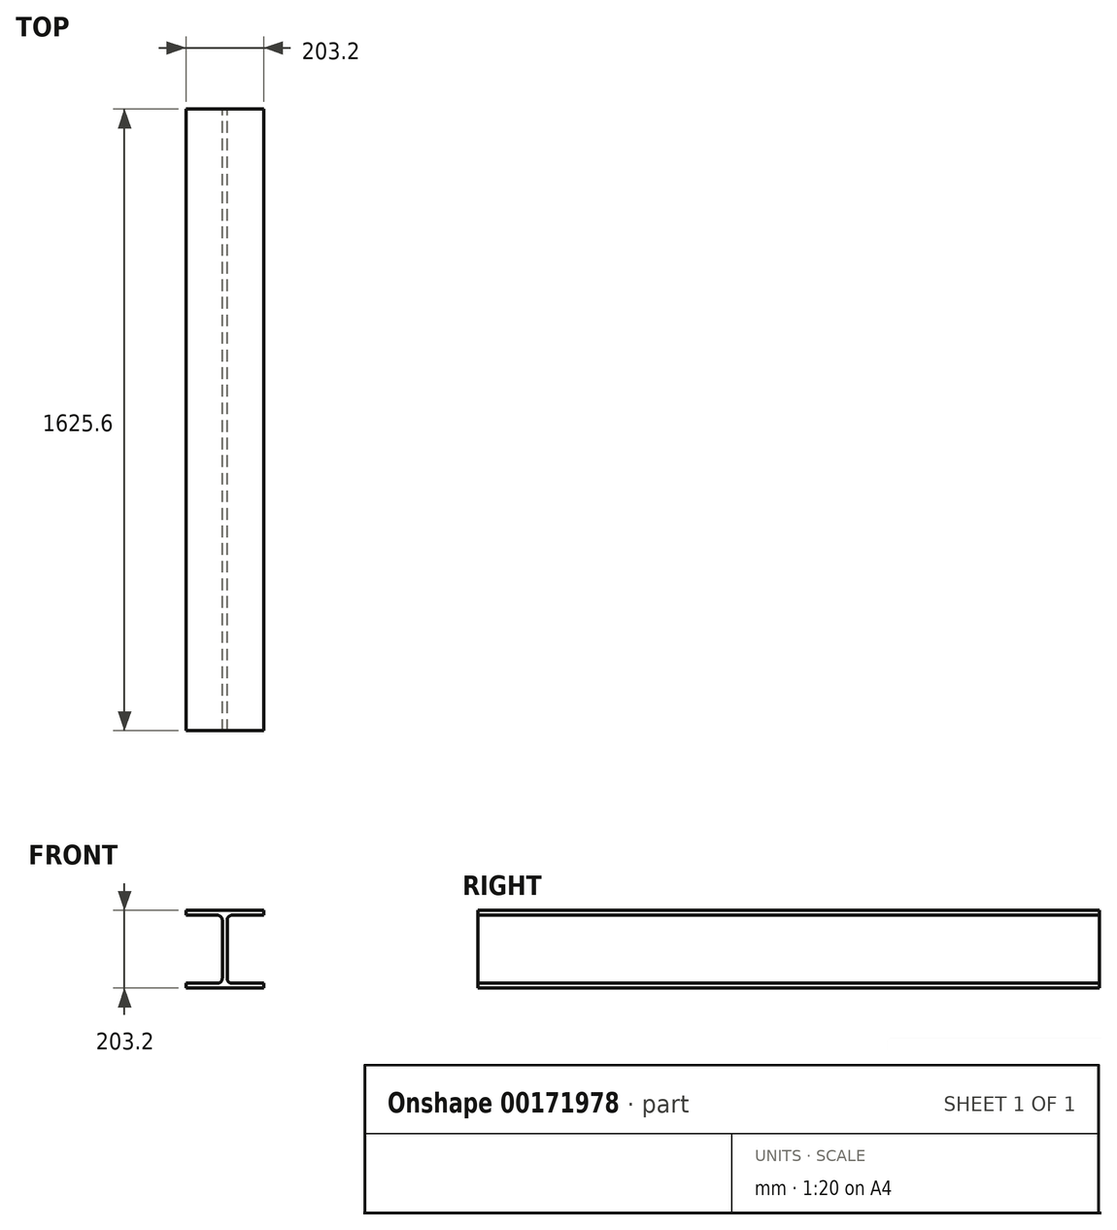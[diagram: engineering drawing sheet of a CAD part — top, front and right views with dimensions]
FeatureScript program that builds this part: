
annotation { "Feature Type Name" : "Feature", "Feature Type Description" : "" }
export const myFeature = defineFeature(function(context is Context, id is Id, definition is map)
    precondition{}
    {
        {
            var Q0;
            Q0=qCreatedBy(makeId("Front.planeOp"),FACE);
            var sketch = newSketch(context, id + "F0", { "sketchPlane" : qUnion([Q0])});
            skLineSegment(sketch, "E0.top", {"start": v(101.6, -101.6) * mm, "end": v(-101.6, -101.6) * mm});
            skLineSegment(sketch, "E0.left", {"start": v(101.6, 101.6) * mm, "end": v(101.6, 88.9) * mm});
            skLineSegment(sketch, "E0.right", {"start": v(-101.6, 101.6) * mm, "end": v(-101.6, 88.9) * mm});
            skPoint(sketch, "E0.middle", {"position": v(0, 0) * mm});
            skLineSegment(sketch, "E1.top", {"start": v(6.35, -101.6) * mm, "end": v(-6.35, -101.6) * mm});
            skLineSegment(sketch, "E1.left", {"start": v(6.35, 88.9) * mm, "end": v(6.35, -88.9) * mm});
            skLineSegment(sketch, "E1.right", {"start": v(-6.35, 88.9) * mm, "end": v(-6.35, -88.9) * mm});
            skLineSegment(sketch, "E2.bottom", {"start": v(-101.6, -101.6) * mm, "end": v(101.6, -101.6) * mm});
            skLineSegment(sketch, "E2.top", {"start": v(-101.6, -88.9) * mm, "end": v(-6.35, -88.9) * mm});
            skLineSegment(sketch, "E2.left", {"start": v(-101.6, -101.6) * mm, "end": v(-101.6, -88.9) * mm});
            skLineSegment(sketch, "E2.right", {"start": v(101.6, -101.6) * mm, "end": v(101.6, -88.9) * mm});
            skLineSegment(sketch, "E3.top", {"start": v(-101.6, 88.9) * mm, "end": v(-6.35, 88.9) * mm});
            skLineSegment(sketch, "E4.trimOffspring", {"start": v(-101.6, -88.9) * mm, "end": v(-101.6, -101.6) * mm});
            skLineSegment(sketch, "E5.trimOffspring", {"start": v(101.6, -88.9) * mm, "end": v(101.6, -101.6) * mm});
            skLineSegment(sketch, "E6.trimOffspring", {"start": v(6.35, -88.9) * mm, "end": v(101.6, -88.9) * mm});
            skLineSegment(sketch, "E7.trimOffspring", {"start": v(6.35, 88.9) * mm, "end": v(101.6, 88.9) * mm});
            skLineSegment(sketch, "E8", {"start": v(-101.6, 101.6) * mm, "end": v(101.6, 101.6) * mm});
            skSolve(sketch);
        }
        {
            var Q0;
            Q0 = qSketchRegion(id + "F0", true);
            extrude(context, id + "F1", {"entities" : qUnion([Q0]), "depth" : 1625.6 * mm});
        }
        {
            var Q0;
            Q0=makeQuery(id+"F1.opExtrude","SWEPT_EDGE",EDGE,{"disambiguationData":[OSD([sQuery(id+"F0.wireOp",EDGE,"E1.right"),sQuery(id+"F0.wireOp",EDGE,"E2.top")])]});
            var Q1;
            Q1=makeQuery(id+"F1.opExtrude","SWEPT_EDGE",EDGE,{"disambiguationData":[OSD([sQuery(id+"F0.wireOp",EDGE,"E1.left"),sQuery(id+"F0.wireOp",EDGE,"E6.trimOffspring")])]});
            var Q2;
            Q2=makeQuery(id+"F1.opExtrude","SWEPT_EDGE",EDGE,{"disambiguationData":[OSD([sQuery(id+"F0.wireOp",EDGE,"E1.left"),sQuery(id+"F0.wireOp",EDGE,"E7.trimOffspring")])]});
            var Q3;
            Q3=makeQuery(id+"F1.opExtrude","SWEPT_EDGE",EDGE,{"disambiguationData":[OSD([sQuery(id+"F0.wireOp",EDGE,"E1.right"),sQuery(id+"F0.wireOp",EDGE,"E3.top")])]});
            fillet(context, id + "F2", {"entities" : qUnion([Q0, Q1, Q2, Q3]), "radius" : 12.7 * mm, "tangentPropagation" : true, "allowEdgeOverflow" : false});
        }
    });
